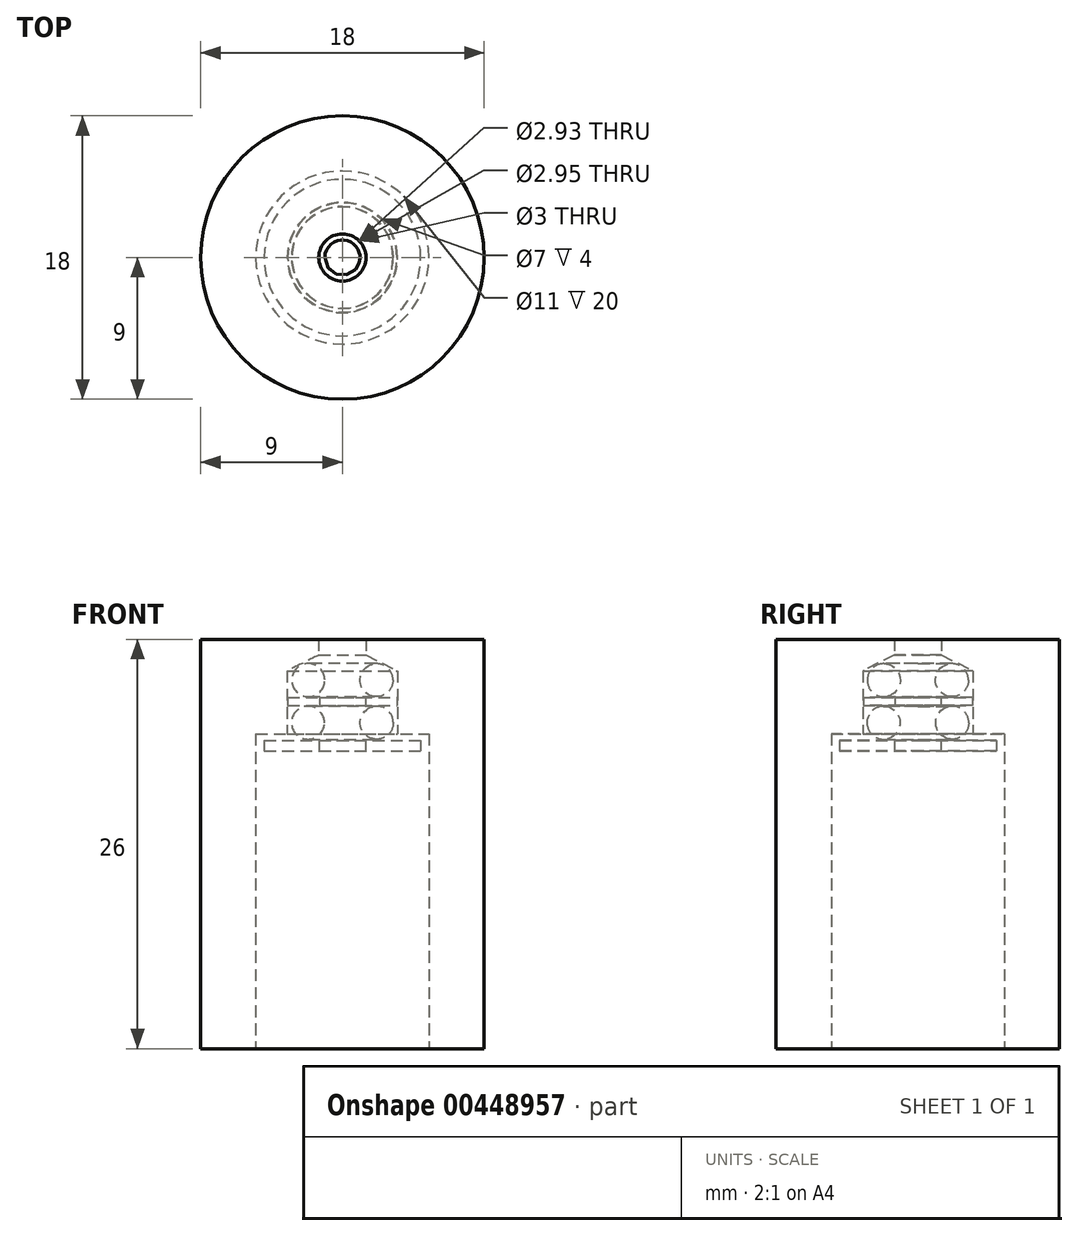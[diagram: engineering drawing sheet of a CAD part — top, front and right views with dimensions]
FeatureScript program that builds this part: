
annotation { "Feature Type Name" : "Feature", "Feature Type Description" : "" }
export const myFeature = defineFeature(function(context is Context, id is Id, definition is map)
    precondition{}
    {
        {
            var Q0;
            Q0=qCreatedBy(makeId("Front.planeOp"),FACE);
            var sketch = newSketch(context, id + "F0", { "sketchPlane" : qUnion([Q0])});
            skLineSegment(sketch, "E0", {"start": v(1.5, 26) * mm, "end": v(1.5, 25) * mm});
            skLineSegment(sketch, "E1", {"start": v(1.5, 25) * mm, "end": v(3.5, 24) * mm});
            skLineSegment(sketch, "E2", {"start": v(3.5, 24) * mm, "end": v(3.5, 20) * mm});
            skLineSegment(sketch, "E3", {"start": v(3.5, 20) * mm, "end": v(5.5, 20) * mm});
            skLineSegment(sketch, "E4", {"start": v(5.5, 20) * mm, "end": v(5.5, 0) * mm});
            skLineSegment(sketch, "E5", {"start": v(5.5, 0) * mm, "end": v(9, 0) * mm});
            skLineSegment(sketch, "E6", {"start": v(9, 0) * mm, "end": v(9, 26) * mm});
            skLineSegment(sketch, "E7", {"start": v(9, 26) * mm, "end": v(1.5, 26) * mm});
            skPoint(sketch, "E8.start.orphan", {"position": v(0, 26) * mm});
            skLineSegment(sketch, "E9", {"start": v(0, -7.67) * mm, "end": v(0, 38.57) * mm, "construction": true});
            skPoint(sketch, "E10.startSnap0", {"position": v(2.5, 24.5) * mm});
            skSolve(sketch);
        }
        {
            var Q0;
            Q0=makeQuery(id+"F0.imprint","IMPRINT",FACE,{"disambiguationData":[TD([[makeQuery(id+"F0.imprint","IMPRINT",EDGE,{"derivedFrom":sQuery(id+"F0.wireOp",EDGE,"E0")}),1.0]])]});
            var Q1;
            Q1=sQuery(id+"F0.wireOp",EDGE,"E7");
            var Q2;
            Q2=sQuery(id+"F0.wireOp",EDGE,"E4");
            var Q3;
            Q3=sQuery(id+"F0.wireOp",EDGE,"E0");
            var Q4;
            Q4=sQuery(id+"F0.wireOp",EDGE,"E1");
            var Q5;
            Q5=sQuery(id+"F0.wireOp",EDGE,"E2");
            var Q6;
            Q6=sQuery(id+"F0.wireOp",EDGE,"E6");
            var Q7;
            Q7=sQuery(id+"F0.wireOp",EDGE,"E9");
            revolve(context, id + "F1", {"entities" : qUnion([Q0]), "surfaceEntities" : qUnion([Q1, Q2, Q3, Q4, Q5, Q6]), "axis" : qUnion([Q7]), "revolveType" : RevolveType.FULL});
        }
        {
            var Q0;
            Q0=qCreatedBy(makeId("Front.planeOp"),FACE);
            var sketch = newSketch(context, id + "F2", { "sketchPlane" : qUnion([Q0])});
            skCircle(sketch, "E11", {"center": v(2.16, 23.4) * mm, "radius": 1.05 * mm});
            skCircle(sketch, "E12", {"center": v(2.18, 20.7) * mm, "radius": 1.05 * mm});
            skLineSegment(sketch, "E13", {"start": v(1.05, 26) * mm, "end": v(1.05, 26) * mm});
            skLineSegment(sketch, "E14.bottom", {"start": v(1.47, 22.3) * mm, "end": v(3.47, 22.3) * mm});
            skLineSegment(sketch, "E14.top", {"start": v(1.47, 21.8) * mm, "end": v(3.47, 21.8) * mm});
            skLineSegment(sketch, "E14.left", {"start": v(1.47, 22.3) * mm, "end": v(1.47, 21.8) * mm});
            skLineSegment(sketch, "E14.right", {"start": v(3.47, 22.3) * mm, "end": v(3.47, 21.8) * mm});
            skLineSegment(sketch, "E15.bottom", {"start": v(4.97, 19.57) * mm, "end": v(1.47, 19.57) * mm});
            skLineSegment(sketch, "E15.top", {"start": v(4.97, 18.92) * mm, "end": v(1.47, 18.92) * mm});
            skLineSegment(sketch, "E15.left", {"start": v(4.97, 19.57) * mm, "end": v(4.97, 18.92) * mm});
            skLineSegment(sketch, "E15.right", {"start": v(1.47, 19.57) * mm, "end": v(1.47, 18.92) * mm});
            skSolve(sketch);
        }
        {
            var Q0;
            Q0 = qSketchRegion(id + "F2", true);
            var Q1;
            Q1=sQuery(id+"F0.wireOp",EDGE,"E9");
            revolve(context, id + "F3", {"entities" : qUnion([Q0]), "axis" : qUnion([Q1]), "revolveType" : RevolveType.FULL});
        }
        {
            var Q0;
            Q0=makeQuery(id+"F2.imprint","IMPRINT",FACE,{"disambiguationData":[TD([[makeQuery(id+"F2.imprint","IMPRINT",EDGE,{"derivedFrom":sQuery(id+"F2.wireOp",EDGE,"E14.bottom")}),-1.0]])]});
            var Q1;
            Q1=sQuery(id+"F2.wireOp",EDGE,"E14.top");
            var Q2;
            Q2=sQuery(id+"F2.wireOp",EDGE,"E14.bottom");
            var Q3;
            Q3=sQuery(id+"F0.wireOp",EDGE,"E9");
            revolve(context, id + "F4", {"entities" : qUnion([Q0]), "surfaceEntities" : qUnion([Q1, Q2]), "axis" : qUnion([Q3]), "revolveType" : RevolveType.FULL});
        }
        {
            var Q0;
            Q0=makeQuery(id+"F2.imprint","IMPRINT",FACE,{"disambiguationData":[TD([[makeQuery(id+"F2.imprint","IMPRINT",EDGE,{"derivedFrom":sQuery(id+"F2.wireOp",EDGE,"E15.bottom")}),1.0]])]});
            var Q1;
            Q1=sQuery(id+"F0.wireOp",EDGE,"E9");
            revolve(context, id + "F5", {"entities" : qUnion([Q0]), "axis" : qUnion([Q1]), "revolveType" : RevolveType.FULL});
        }
        {
            var Q0;
            Q0=makeQuery(id+"F4.opRevolve","SWEPT_BODY",BODY,{"disambiguationData":[OSD([sQuery(id+"F2.wireOp",EDGE,"E14.bottom"),sQuery(id+"F2.wireOp",EDGE,"E14.top"),sQuery(id+"F2.wireOp",EDGE,"E14.left"),sQuery(id+"F2.wireOp",EDGE,"E14.right")])]});
            deleteBodies(context, id + "F6", {"entities" : qUnion([Q0])});
        }
        {
            var Q0;
            Q0=makeQuery(id+"F5.opRevolve","SWEPT_BODY",BODY,{"disambiguationData":[OSD([sQuery(id+"F2.wireOp",EDGE,"E15.bottom"),sQuery(id+"F2.wireOp",EDGE,"E15.top"),sQuery(id+"F2.wireOp",EDGE,"E15.left"),sQuery(id+"F2.wireOp",EDGE,"E15.right")])]});
            deleteBodies(context, id + "F7", {"entities" : qUnion([Q0])});
        }
    });
